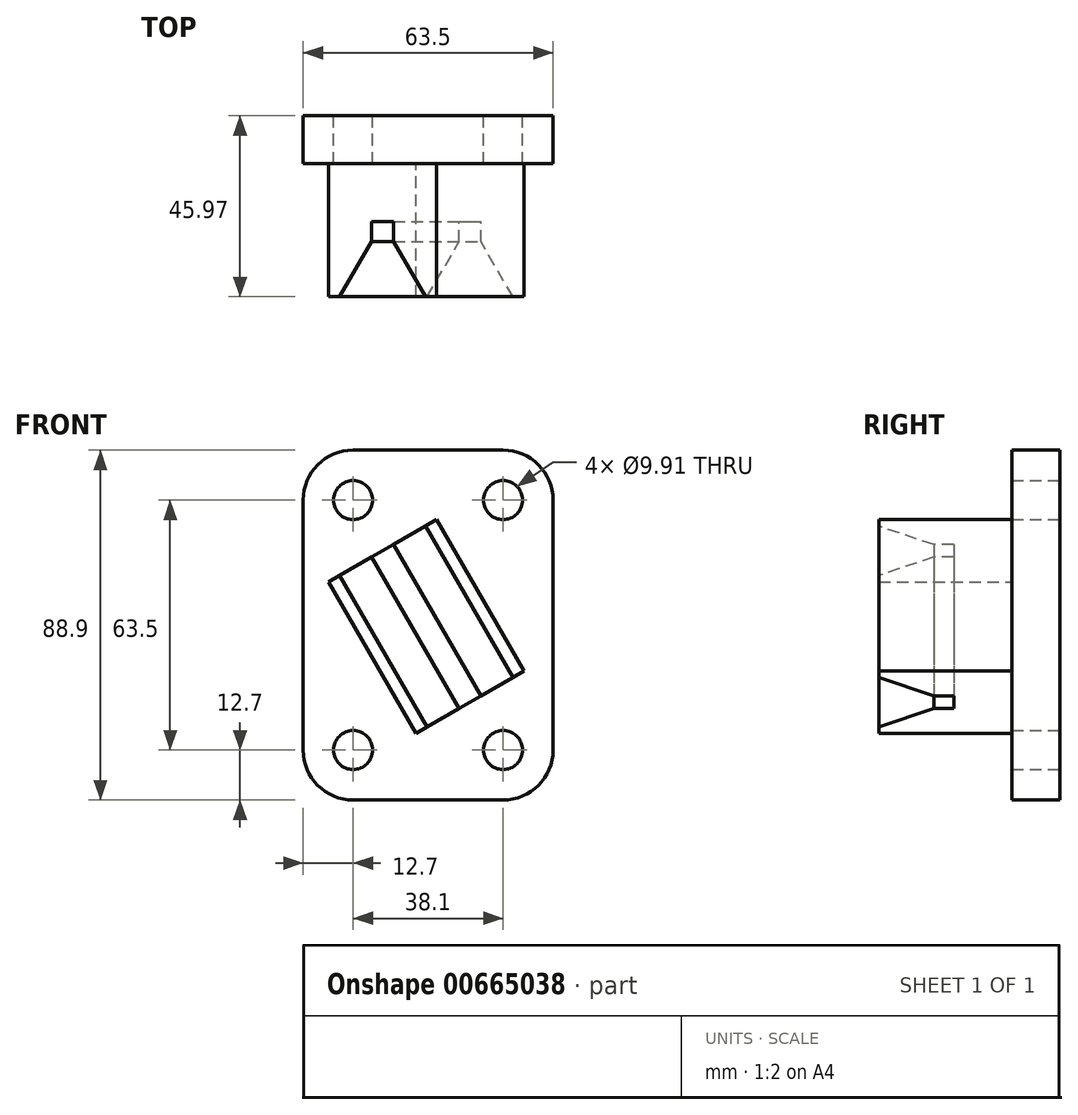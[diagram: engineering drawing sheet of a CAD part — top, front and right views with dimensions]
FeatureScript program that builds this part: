
annotation { "Feature Type Name" : "Feature", "Feature Type Description" : "" }
export const myFeature = defineFeature(function(context is Context, id is Id, definition is map)
    precondition{}
    {
        {
            var Q0;
            Q0=qCreatedBy(makeId("Front.planeOp"),FACE);
            var sketch = newSketch(context, id + "F0", { "sketchPlane" : qUnion([Q0])});
            skLineSegment(sketch, "E0", {"start": v(12.7, 0) * mm, "end": v(50.8, 0) * mm});
            skLineSegment(sketch, "E1", {"start": v(63.5, -12.7) * mm, "end": v(63.5, -76.2) * mm});
            skLineSegment(sketch, "E2", {"start": v(50.8, -88.9) * mm, "end": v(12.7, -88.9) * mm});
            skLineSegment(sketch, "E3", {"start": v(0, -76.2) * mm, "end": v(0, -12.7) * mm});
            skPoint(sketch, "E4.visualSharp", {"position": v(63.5, 0) * mm});
            skArc(sketch, "E4.filletArc", {"start": v(63.5, -12.7) * mm, "mid": v(59.78, -3.72) * mm, "end": v(50.8, 0) * mm});
            skPoint(sketch, "E5.visualSharp", {"position": v(63.5, -88.9) * mm});
            skArc(sketch, "E5.filletArc", {"start": v(50.8, -88.9) * mm, "mid": v(59.78, -85.18) * mm, "end": v(63.5, -76.2) * mm});
            skPoint(sketch, "E6.visualSharp", {"position": v(0, -88.9) * mm});
            skArc(sketch, "E6.filletArc", {"start": v(0, -76.2) * mm, "mid": v(3.72, -85.18) * mm, "end": v(12.7, -88.9) * mm});
            skPoint(sketch, "E7.visualSharp", {"position": v(0, 0) * mm});
            skArc(sketch, "E7.filletArc", {"start": v(12.7, 0) * mm, "mid": v(3.72, -3.72) * mm, "end": v(0, -12.7) * mm});
            skCircle(sketch, "E8", {"center": v(50.8, -76.2) * mm, "radius": 4.95 * mm});
            skCircle(sketch, "E9", {"center": v(12.7, -76.2) * mm, "radius": 4.95 * mm});
            skLineSegment(sketch, "E10", {"start": v(33.9, -17.64) * mm, "end": v(56.13, -56.13) * mm});
            skCircle(sketch, "E11", {"center": v(12.7, -12.7) * mm, "radius": 4.95 * mm});
            skCircle(sketch, "E12", {"center": v(50.8, -12.7) * mm, "radius": 4.95 * mm});
            skLineSegment(sketch, "E13.0", {"start": v(6.41, -33.52) * mm, "end": v(28.64, -72) * mm});
            skLineSegment(sketch, "E14", {"start": v(6.41, -33.52) * mm, "end": v(33.9, -17.64) * mm});
            skLineSegment(sketch, "E15", {"start": v(28.64, -72) * mm, "end": v(56.13, -56.13) * mm});
            skLineSegment(sketch, "E16.0", {"start": v(22.91, -24) * mm, "end": v(45.14, -62.48) * mm});
            skLineSegment(sketch, "E17.0", {"start": v(17.41, -27.17) * mm, "end": v(39.64, -65.66) * mm});
            skLineSegment(sketch, "E18.0", {"start": v(9.27, -31.86) * mm, "end": v(31.5, -70.36) * mm});
            skLineSegment(sketch, "E19.0", {"start": v(31.05, -19.3) * mm, "end": v(53.27, -57.79) * mm});
            skSolve(sketch);
        }
        {
            var Q0;
            Q0=makeQuery(id+"F0.imprint","IMPRINT",FACE,{"disambiguationData":[TD([[makeQuery(id+"F0.imprint","IMPRINT",EDGE,{"derivedFrom":sQuery(id+"F0.wireOp",EDGE,"E0")}),-1.0]])]});
            extrude(context, id + "F1", {"entities" : qUnion([Q0]), "depth" : 12.2 * mm, "offsetDistance" : 25.4 * mm});
        }
        {
            var Q0;
            {var subQ0=sQuery(id+"F0.wireOp",EDGE,"E10");Q0=makeQuery(id+"F0.imprint","IMPRINT",FACE,{"disambiguationData":[TD([[makeQuery(id+"F0.imprint","IMPRINT",EDGE,{"derivedFrom":subQ0}),-1.0]])]});}
            var Q1;
            {var subQ0=sQuery(id+"F0.wireOp",EDGE,"E16.0");Q1=makeQuery(id+"F0.imprint","IMPRINT",FACE,{"disambiguationData":[TD([[makeQuery(id+"F0.imprint","IMPRINT",EDGE,{"derivedFrom":subQ0}),1.0]])]});}
            var Q2;
            {var subQ0=sQuery(id+"F0.wireOp",EDGE,"E16.0");Q2=makeQuery(id+"F0.imprint","IMPRINT",FACE,{"disambiguationData":[TD([[makeQuery(id+"F0.imprint","IMPRINT",EDGE,{"derivedFrom":subQ0}),-1.0]])]});}
            var Q3;
            {var subQ0=sQuery(id+"F0.wireOp",EDGE,"E17.0");Q3=makeQuery(id+"F0.imprint","IMPRINT",FACE,{"disambiguationData":[TD([[makeQuery(id+"F0.imprint","IMPRINT",EDGE,{"derivedFrom":subQ0}),-1.0]])]});}
            var Q4;
            {var subQ0=sQuery(id+"F0.wireOp",EDGE,"E13.0");Q4=makeQuery(id+"F0.imprint","IMPRINT",FACE,{"disambiguationData":[TD([[makeQuery(id+"F0.imprint","IMPRINT",EDGE,{"derivedFrom":subQ0}),1.0]])]});}
            extrude(context, id + "F2", {"entities" : qUnion([Q0, Q1, Q2, Q3, Q4]), "operationType" : NewBodyOperationType.ADD, "depth" : 45.97 * mm, "offsetDistance" : 25.4 * mm});
        }
        {
            var Q0;
            Q0=makeQuery(id+"F2.opExtrude","SWEPT_FACE",FACE,{"disambiguationData":[OSD([sQuery(id+"F0.wireOp",EDGE,"E15")])]});
            var sketch = newSketch(context, id + "F3", { "sketchPlane" : qUnion([Q0])});
            skLineSegment(sketch, "E20.0", {"start": v(1.5, 32) * mm, "end": v(1.5, 26.92) * mm});
            skLineSegment(sketch, "E21.0", {"start": v(7.85, 32) * mm, "end": v(7.85, 26.92) * mm});
            skLineSegment(sketch, "E22.trimOffspring", {"start": v(1.5, 26.92) * mm, "end": v(7.85, 26.92) * mm});
            skLineSegment(sketch, "E23", {"start": v(-7.9, 45.97) * mm, "end": v(1.5, 32) * mm});
            skLineSegment(sketch, "E24", {"start": v(17.24, 45.97) * mm, "end": v(7.85, 32) * mm});
            skLineSegment(sketch, "E25", {"start": v(17.24, 45.97) * mm, "end": v(20.55, 45.97) * mm});
            skLineSegment(sketch, "E26", {"start": v(-7.9, 45.97) * mm, "end": v(-11.2, 45.97) * mm});
            skSolve(sketch);
        }
        {
            var Q0;
            Q0=makeQuery(id+"F3.imprint","IMPRINT",FACE,{"disambiguationData":[TD([[makeQuery(id+"F3.imprint","IMPRINT",EDGE,{"derivedFrom":sQuery(id+"F3.wireOp",EDGE,"E20.0")}),1.0]])]});
            extrude(context, id + "F4", {"entities" : qUnion([Q0]), "operationType" : NewBodyOperationType.REMOVE, "oppositeDirection" : true, "depth" : 203.2 * mm, "offsetDistance" : 25.4 * mm});
        }
    });
